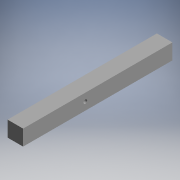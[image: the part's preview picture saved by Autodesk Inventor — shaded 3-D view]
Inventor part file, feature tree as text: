
AUTODESK INVENTOR PART (.ipt)
format: ipt  version: 2019 (Build 230136000, 136)  size: 96,256 bytes
history: native  units: mm (DEFAULTED — no unit token found)
features: extrude x2, sketch x2
ambient origin geometry x8: Origin, YZ Plane, XZ Plane, XY Plane, X Axis, Y Axis, Z Axis, Center Point
bodies: Solid1 (feature_tree)
feature tree (4):
  extrude  "Extrusion1"  Depth=31.75mm
  extrude  "Extrusion2"  Depth=31.75mm
  sketch  "Sketch1"  dims[d0=31.75mm d1=31.75mm]
  sketch  "Sketch2"  dims[d2=304.8mm d3=0.0mm d4=177.8mm d5=31.75mm d6=15.875mm d7=7.62mm d8=120.0mm d9=0.0mm]
